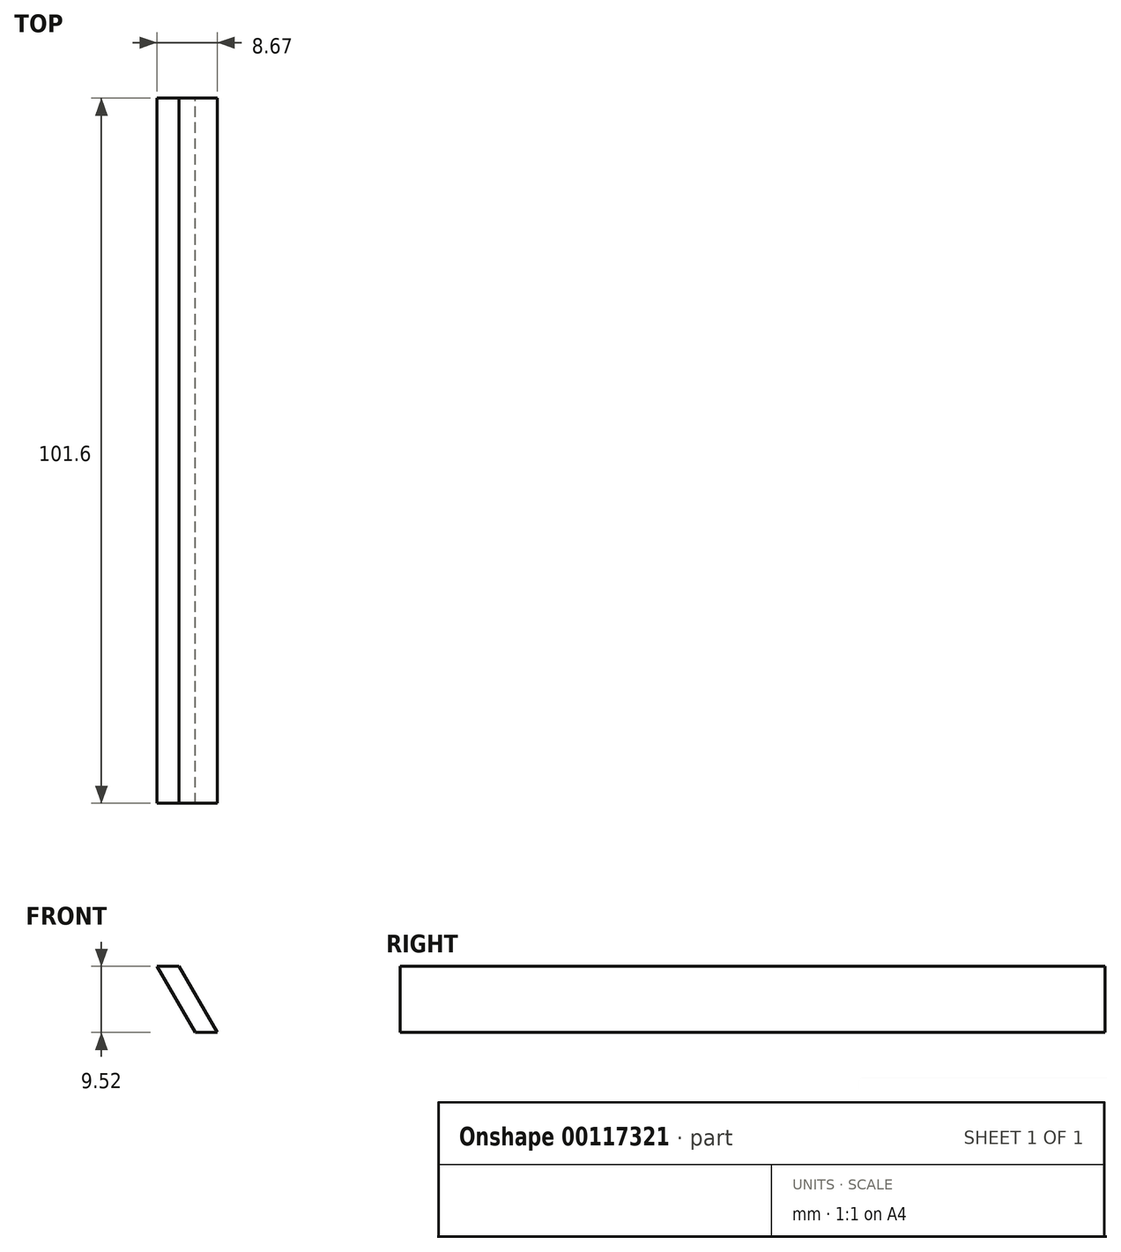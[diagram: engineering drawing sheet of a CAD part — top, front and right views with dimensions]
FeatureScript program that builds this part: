
annotation { "Feature Type Name" : "Feature", "Feature Type Description" : "" }
export const myFeature = defineFeature(function(context is Context, id is Id, definition is map)
    precondition{}
    {
        {
            var Q0;
            Q0=qCreatedBy(makeId("Front.planeOp"),FACE);
            var sketch = newSketch(context, id + "F0", { "sketchPlane" : qUnion([Q0])});
            skLineSegment(sketch, "E0", {"start": v(-5.5, 2.38) * mm, "end": v(0, -7.14) * mm});
            skLineSegment(sketch, "E1", {"start": v(0, -7.14) * mm, "end": v(3.17, -7.14) * mm});
            skLineSegment(sketch, "E2", {"start": v(3.17, -7.14) * mm, "end": v(-2.32, 2.38) * mm});
            skLineSegment(sketch, "E3", {"start": v(-2.32, 2.38) * mm, "end": v(-5.5, 2.38) * mm});
            skSolve(sketch);
        }
        {
            var Q0;
            Q0=makeQuery(id+"F0.imprint","IMPRINT",FACE,{"disambiguationData":[TD([[makeQuery(id+"F0.imprint","IMPRINT",EDGE,{"derivedFrom":sQuery(id+"F0.wireOp",EDGE,"E0")}),1.0]])]});
            extrude(context, id + "F1", {"entities" : qUnion([Q0]), "depth" : 101.6 * mm});
        }
    });
